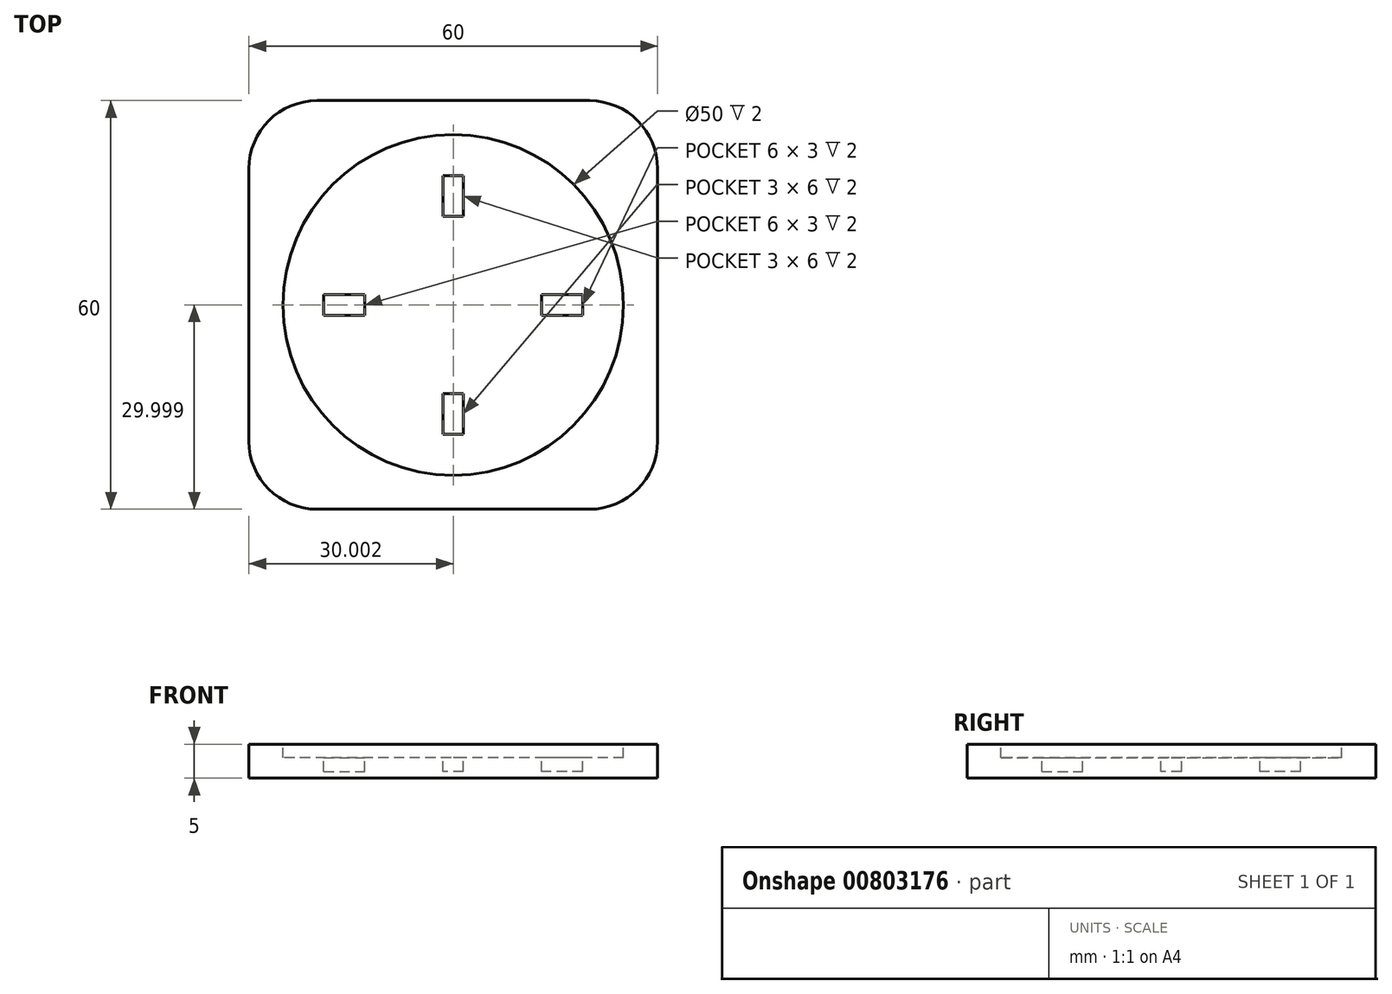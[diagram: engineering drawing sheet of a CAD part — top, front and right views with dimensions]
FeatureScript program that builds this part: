
annotation { "Feature Type Name" : "Feature", "Feature Type Description" : "" }
export const myFeature = defineFeature(function(context is Context, id is Id, definition is map)
    precondition{}
    {
        {
            var Q0;
            Q0=qCreatedBy(makeId("Top.planeOp"),FACE);
            var sketch = newSketch(context, id + "F0", { "sketchPlane" : qUnion([Q0])});
            skLineSegment(sketch, "E0.bottom", {"start": v(-30.29, 37.73) * mm, "end": v(29.71, 37.73) * mm});
            skLineSegment(sketch, "E0.top", {"start": v(-30.29, -22.27) * mm, "end": v(29.71, -22.27) * mm});
            skLineSegment(sketch, "E0.left", {"start": v(-30.29, 37.73) * mm, "end": v(-30.29, -22.27) * mm});
            skLineSegment(sketch, "E0.right", {"start": v(29.71, 37.73) * mm, "end": v(29.71, -22.27) * mm});
            skSolve(sketch);
        }
        {
            var Q0;
            Q0 = qSketchRegion(id + "F0", true);
            extrude(context, id + "F1", {"entities" : qUnion([Q0]), "depth" : 5 * mm, "offsetDistance" : 25.4 * mm});
        }
        {
            var Q0;
            Q0=makeQuery(id+"F1.opExtrude","CAP_FACE",FACE,{"disambiguationData":[OSD([sQuery(id+"F0.wireOp",EDGE,"E0.bottom"),sQuery(id+"F0.wireOp",EDGE,"E0.top"),sQuery(id+"F0.wireOp",EDGE,"E0.left"),sQuery(id+"F0.wireOp",EDGE,"E0.right")])],"isStart":false});
            var sketch = newSketch(context, id + "F2", { "sketchPlane" : qUnion([Q0])});
            skCircle(sketch, "E1", {"center": v(-0.29, 7.73) * mm, "radius": 25 * mm});
            skSolve(sketch);
        }
        {
            var Q0;
            Q0 = qSketchRegion(id + "F2", true);
            extrude(context, id + "F3", {"entities" : qUnion([Q0]), "operationType" : NewBodyOperationType.REMOVE, "oppositeDirection" : true, "depth" : 2 * mm, "offsetDistance" : 25.4 * mm});
        }
        {
            var Q0;
            Q0=makeQuery(id+"F1.opExtrude","SWEPT_EDGE",EDGE,{"disambiguationData":[OSD([sQuery(id+"F0.wireOp",EDGE,"E0.top"),sQuery(id+"F0.wireOp",EDGE,"E0.right")])]});
            var Q1;
            Q1=makeQuery(id+"F1.opExtrude","SWEPT_EDGE",EDGE,{"disambiguationData":[OSD([sQuery(id+"F0.wireOp",EDGE,"E0.bottom"),sQuery(id+"F0.wireOp",EDGE,"E0.right")])]});
            var Q2;
            Q2=makeQuery(id+"F1.opExtrude","SWEPT_EDGE",EDGE,{"disambiguationData":[OSD([sQuery(id+"F0.wireOp",EDGE,"E0.bottom"),sQuery(id+"F0.wireOp",EDGE,"E0.left")])]});
            var Q3;
            Q3=makeQuery(id+"F1.opExtrude","SWEPT_EDGE",EDGE,{"disambiguationData":[OSD([sQuery(id+"F0.wireOp",EDGE,"E0.top"),sQuery(id+"F0.wireOp",EDGE,"E0.left")])]});
            fillet(context, id + "F4", {"entities" : qUnion([Q0, Q1, Q2, Q3]), "radius" : 10 * mm, "tangentPropagation" : true, "allowEdgeOverflow" : false});
        }
        {
            var Q0;
            Q0=makeQuery(id+"F3.boolean.opBoolean","COPY",FACE,{"derivedFrom":makeQuery(id+"F3.opExtrude","CAP_FACE",FACE,{"disambiguationData":[OSD([sQuery(id+"F2.wireOp",EDGE,"E1")])],"isStart":false})});
            var sketch = newSketch(context, id + "F5", { "sketchPlane" : qUnion([Q0])});
            skLineSegment(sketch, "E2.bottom", {"start": v(-1.79, 26.73) * mm, "end": v(1.21, 26.73) * mm});
            skLineSegment(sketch, "E2.top", {"start": v(-1.79, 20.73) * mm, "end": v(1.21, 20.73) * mm});
            skLineSegment(sketch, "E2.left", {"start": v(-1.79, 26.73) * mm, "end": v(-1.79, 20.73) * mm});
            skLineSegment(sketch, "E2.right", {"start": v(1.21, 26.73) * mm, "end": v(1.21, 20.73) * mm});
            skLineSegment(sketch, "E3.1.0", {"start": v(-19.29, 6.23) * mm, "end": v(-13.29, 6.23) * mm});
            skLineSegment(sketch, "E3.1.1", {"start": v(-19.29, 9.23) * mm, "end": v(-13.29, 9.23) * mm});
            skLineSegment(sketch, "E3.1.2", {"start": v(-19.29, 6.23) * mm, "end": v(-19.29, 9.23) * mm});
            skLineSegment(sketch, "E3.1.3", {"start": v(-13.29, 6.23) * mm, "end": v(-13.29, 9.23) * mm});
            skLineSegment(sketch, "E3.2.0", {"start": v(1.21, -11.27) * mm, "end": v(1.21, -5.27) * mm});
            skLineSegment(sketch, "E3.2.1", {"start": v(-1.79, -11.27) * mm, "end": v(-1.79, -5.27) * mm});
            skLineSegment(sketch, "E3.2.2", {"start": v(1.21, -11.27) * mm, "end": v(-1.79, -11.27) * mm});
            skLineSegment(sketch, "E3.2.3", {"start": v(1.21, -5.27) * mm, "end": v(-1.79, -5.27) * mm});
            skLineSegment(sketch, "E3.3.0", {"start": v(18.71, 9.23) * mm, "end": v(12.71, 9.23) * mm});
            skLineSegment(sketch, "E3.3.1", {"start": v(18.71, 6.23) * mm, "end": v(12.71, 6.23) * mm});
            skLineSegment(sketch, "E3.3.2", {"start": v(18.71, 9.23) * mm, "end": v(18.71, 6.23) * mm});
            skLineSegment(sketch, "E3.3.3", {"start": v(12.71, 9.23) * mm, "end": v(12.71, 6.23) * mm});
            skPoint(sketch, "E3.center", {"position": v(-0.29, 7.73) * mm});
            skSolve(sketch);
        }
        {
            var Q0;
            Q0 = qSketchRegion(id + "F5", true);
            extrude(context, id + "F6", {"entities" : qUnion([Q0]), "operationType" : NewBodyOperationType.REMOVE, "oppositeDirection" : true, "depth" : 2 * mm, "offsetDistance" : 25.4 * mm});
        }
    });
